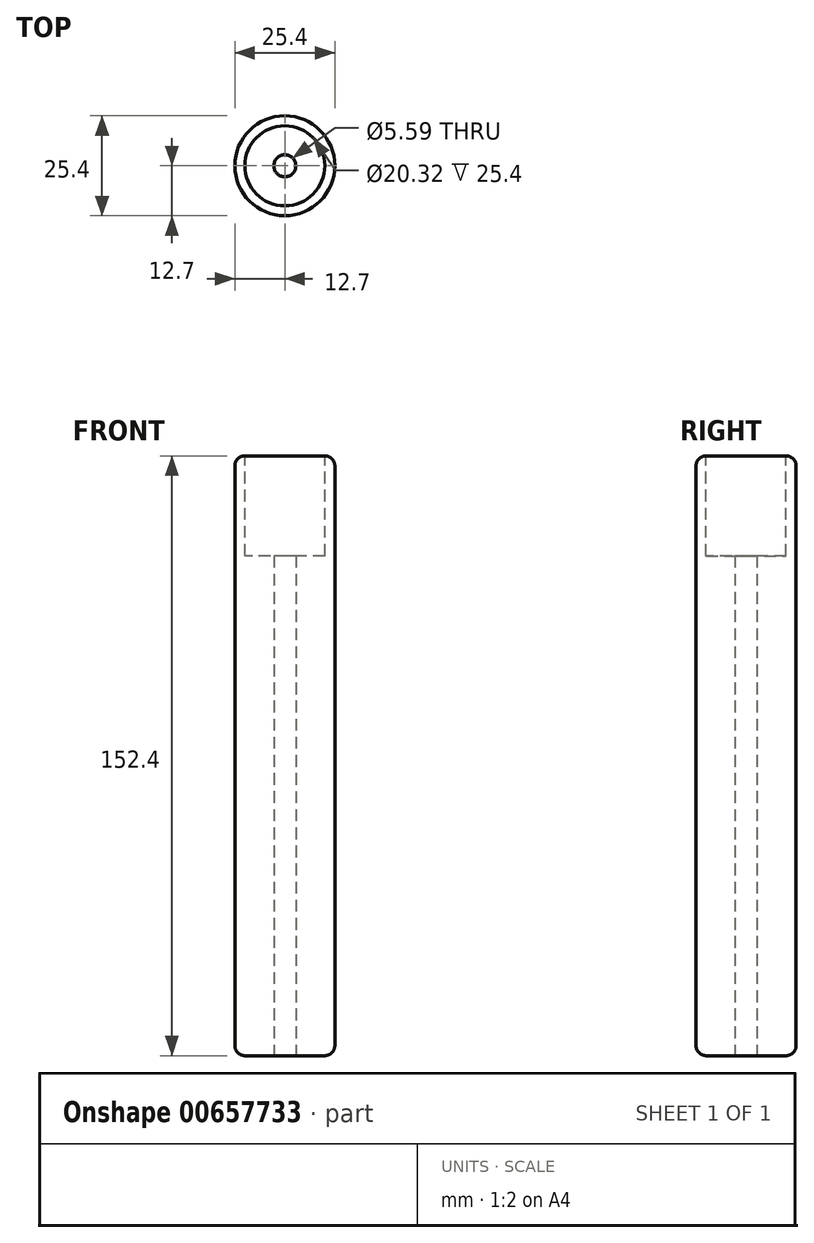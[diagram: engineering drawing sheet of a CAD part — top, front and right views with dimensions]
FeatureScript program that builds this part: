
annotation { "Feature Type Name" : "Feature", "Feature Type Description" : "" }
export const myFeature = defineFeature(function(context is Context, id is Id, definition is map)
    precondition{}
    {
        {
            var Q0;
            Q0=qCreatedBy(makeId("Top.planeOp"),FACE);
            var sketch = newSketch(context, id + "F0", { "sketchPlane" : qUnion([Q0])});
            skCircle(sketch, "E0", {"center": v(0, 0) * mm, "radius": 12.7 * mm});
            skSolve(sketch);
        }
        {
            var Q0;
            Q0=makeQuery(id+"F0.imprint","IMPRINT",FACE,{"disambiguationData":[TD([[makeQuery(id+"F0.imprint","IMPRINT",EDGE,{"derivedFrom":sQuery(id+"F0.wireOp",EDGE,"E0")}),1.0]])]});
            var sketch = newSketch(context, id + "F1", { "sketchPlane" : qUnion([Q0])});
            skCircle(sketch, "E1", {"center": v(0, 0) * mm, "radius": 2.8 * mm});
            skSolve(sketch);
        }
        {
            var Q0;
            Q0=makeQuery(id+"F0.imprint","IMPRINT",FACE,{"disambiguationData":[TD([[makeQuery(id+"F0.imprint","IMPRINT",EDGE,{"derivedFrom":sQuery(id+"F0.wireOp",EDGE,"E0")}),1.0]])]});
            extrude(context, id + "F2", {"entities" : qUnion([Q0]), "depth" : 152.4 * mm, "offsetDistance" : 25.4 * mm});
        }
        {
            var Q0;
            Q0=makeQuery(id+"F1.imprint","IMPRINT",FACE,{"disambiguationData":[TD([[makeQuery(id+"F1.imprint","IMPRINT",EDGE,{"derivedFrom":sQuery(id+"F1.wireOp",EDGE,"E1")}),1.0]])]});
            var Q1;
            Q1=sQuery(id+"F1.wireOp",EDGE,"E1");
            extrude(context, id + "F3", {"entities" : qUnion([Q0]), "operationType" : NewBodyOperationType.REMOVE, "surfaceEntities" : qUnion([Q1]), "oppositeDirection" : true, "depth" : -177.8 * mm, "offsetDistance" : 25.4 * mm});
        }
        {
            var Q0;
            Q0=makeQuery(id+"F2.opExtrude","CAP_EDGE",EDGE,{"disambiguationData":[OSD([sQuery(id+"F0.wireOp",EDGE,"E0")])],"isStart":true});
            fillet(context, id + "F4", {"entities" : qUnion([Q0]), "radius" : 2.54 * mm, "tangentPropagation" : true, "allowEdgeOverflow" : false});
        }
        {
            var Q0;
            Q0=makeQuery(id+"F2.opExtrude","CAP_EDGE",EDGE,{"disambiguationData":[OSD([sQuery(id+"F0.wireOp",EDGE,"E0")])],"isStart":false});
            fillet(context, id + "F5", {"entities" : qUnion([Q0]), "radius" : 2.54 * mm, "tangentPropagation" : true, "allowEdgeOverflow" : false});
        }
        {
            var Q0;
            Q0=makeQuery(id+"F2.opExtrude","CAP_FACE",FACE,{"disambiguationData":[OSD([sQuery(id+"F0.wireOp",EDGE,"E0")])],"isStart":false});
            extrude(context, id + "F6", {"entities" : qUnion([Q0]), "operationType" : NewBodyOperationType.REMOVE, "oppositeDirection" : true, "depth" : 25.4 * mm, "offsetDistance" : 25.4 * mm});
        }
    });
